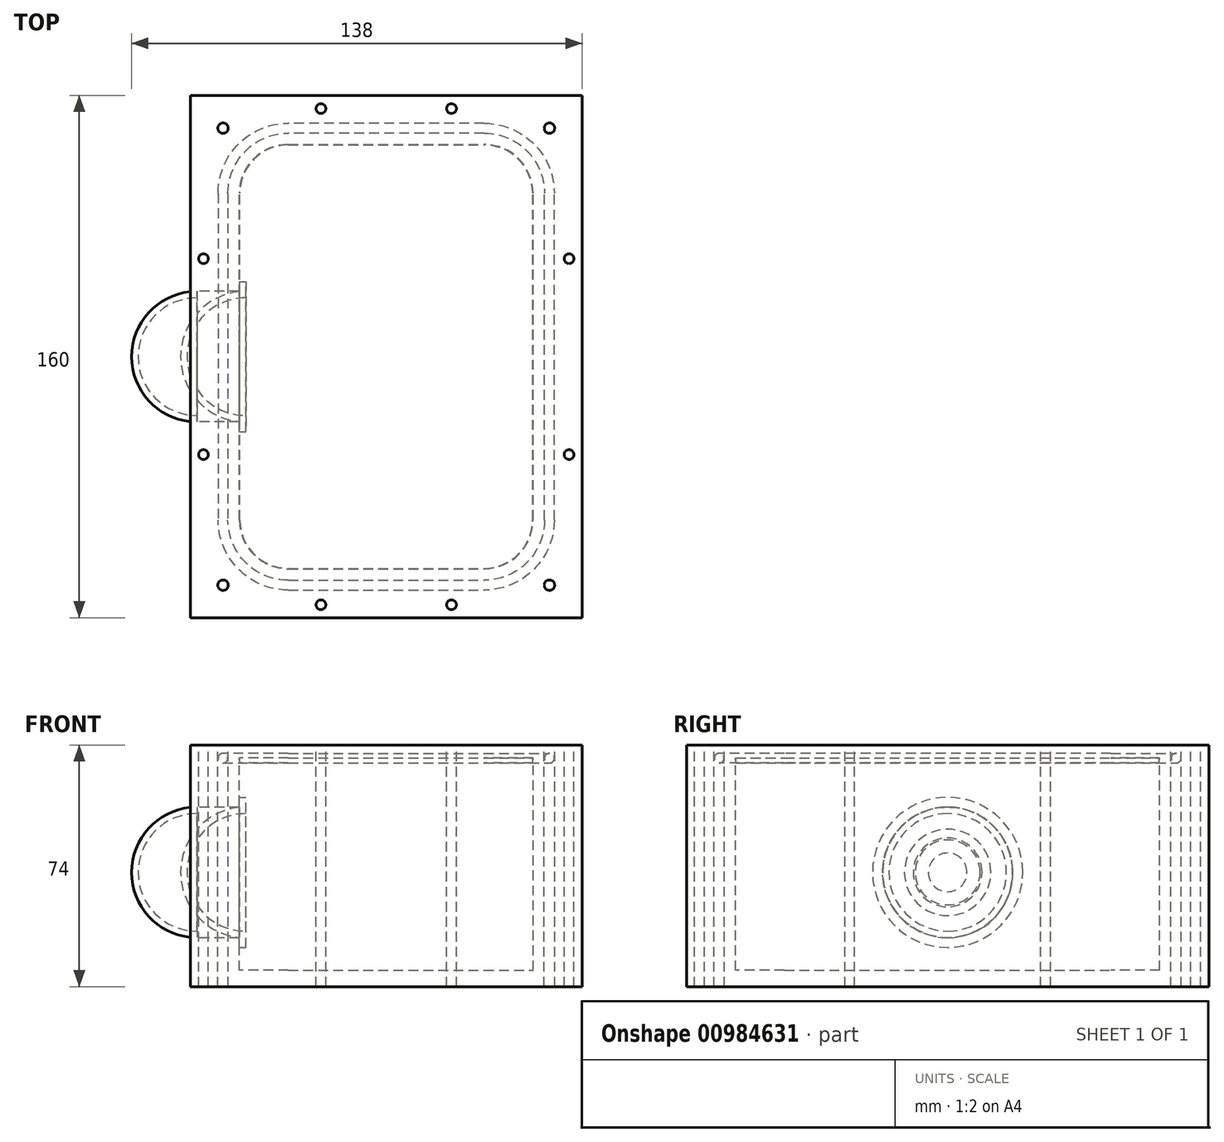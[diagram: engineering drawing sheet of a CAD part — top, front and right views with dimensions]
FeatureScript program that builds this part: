
annotation { "Feature Type Name" : "Feature", "Feature Type Description" : "" }
export const myFeature = defineFeature(function(context is Context, id is Id, definition is map)
    precondition{}
    {
        {
            var Q0;
            Q0=qCreatedBy(makeId("Top.planeOp"),FACE);
            var sketch = newSketch(context, id + "F0", { "sketchPlane" : qUnion([Q0])});
            skLineSegment(sketch, "E0.bottom", {"start": v(-60, -80) * mm, "end": v(60, -80) * mm});
            skLineSegment(sketch, "E0.top", {"start": v(-60, 80) * mm, "end": v(60, 80) * mm});
            skLineSegment(sketch, "E0.left", {"start": v(-60, -80) * mm, "end": v(-60, 80) * mm});
            skLineSegment(sketch, "E0.right", {"start": v(60, -80) * mm, "end": v(60, 80) * mm});
            skSolve(sketch);
        }
        {
            var Q0;
            Q0 = qSketchRegion(id + "F0", true);
            extrude(context, id + "F1", {"entities" : qUnion([Q0]), "oppositeDirection" : true, "depth" : 70 * mm, "offsetDistance" : 25 * mm});
        }
        {
            var Q0;
            Q0=qCreatedBy(makeId("Top.planeOp"),FACE);
            var sketch = newSketch(context, id + "F2", { "sketchPlane" : qUnion([Q0])});
            skLineSegment(sketch, "E1.bottom", {"start": v(-45, -65) * mm, "end": v(45, -65) * mm});
            skLineSegment(sketch, "E1.top", {"start": v(-45, 65) * mm, "end": v(45, 65) * mm});
            skLineSegment(sketch, "E1.left", {"start": v(-45, -65) * mm, "end": v(-45, 65) * mm});
            skLineSegment(sketch, "E1.right", {"start": v(45, -65) * mm, "end": v(45, 65) * mm});
            skSolve(sketch);
        }
        {
            var Q0;
            Q0=makeQuery(id+"F2.imprint","IMPRINT",FACE,{"disambiguationData":[TD([[makeQuery(id+"F2.imprint","IMPRINT",EDGE,{"derivedFrom":sQuery(id+"F2.wireOp",EDGE,"E1.bottom")}),1.0]])]});
            extrude(context, id + "F3", {"entities" : qUnion([Q0]), "operationType" : NewBodyOperationType.REMOVE, "oppositeDirection" : true, "depth" : 65 * mm, "offsetDistance" : 25 * mm});
        }
        {
            var Q0;
            Q0=makeQuery(id+"F3.boolean.opBoolean","COPY",EDGE,{"derivedFrom":makeQuery(id+"F3.opExtrude","SWEPT_EDGE",EDGE,{"disambiguationData":[OSD([sQuery(id+"F2.wireOp",EDGE,"E1.bottom"),sQuery(id+"F2.wireOp",EDGE,"E1.left")])]})});
            var Q1;
            Q1=makeQuery(id+"F3.boolean.opBoolean","COPY",EDGE,{"derivedFrom":makeQuery(id+"F3.opExtrude","SWEPT_EDGE",EDGE,{"disambiguationData":[OSD([sQuery(id+"F2.wireOp",EDGE,"E1.bottom"),sQuery(id+"F2.wireOp",EDGE,"E1.right")])]})});
            var Q2;
            Q2=makeQuery(id+"F3.boolean.opBoolean","COPY",EDGE,{"derivedFrom":makeQuery(id+"F3.opExtrude","SWEPT_EDGE",EDGE,{"disambiguationData":[OSD([sQuery(id+"F2.wireOp",EDGE,"E1.top"),sQuery(id+"F2.wireOp",EDGE,"E1.right")])]})});
            var Q3;
            Q3=makeQuery(id+"F3.boolean.opBoolean","COPY",EDGE,{"derivedFrom":makeQuery(id+"F3.opExtrude","SWEPT_EDGE",EDGE,{"disambiguationData":[OSD([sQuery(id+"F2.wireOp",EDGE,"E1.top"),sQuery(id+"F2.wireOp",EDGE,"E1.left")])]})});
            fillet(context, id + "F4", {"entities" : qUnion([Q0, Q1, Q2, Q3]), "radius" : 15 * mm, "tangentPropagation" : true, "allowEdgeOverflow" : false});
        }
        {
            var Q0;
            Q0=makeQuery(id+"F1.opExtrude","CAP_FACE",FACE,{"disambiguationData":[OSD([sQuery(id+"F0.wireOp",EDGE,"E0.bottom"),sQuery(id+"F0.wireOp",EDGE,"E0.top"),sQuery(id+"F0.wireOp",EDGE,"E0.left"),sQuery(id+"F0.wireOp",EDGE,"E0.right")])],"isStart":true});
            var sketch = newSketch(context, id + "F5", { "sketchPlane" : qUnion([Q0])});
            skArc(sketch, "E2.0", {"start": v(-30, -70) * mm, "mid": v(-44.14, -64.14) * mm, "end": v(-50, -50) * mm});
            skLineSegment(sketch, "E2.1", {"start": v(-30, -70) * mm, "end": v(30, -70) * mm});
            skLineSegment(sketch, "E2.2", {"start": v(-50, -50) * mm, "end": v(-50, 50) * mm});
            skArc(sketch, "E2.3", {"start": v(50, -50) * mm, "mid": v(44.14, -64.14) * mm, "end": v(30, -70) * mm});
            skArc(sketch, "E2.4", {"start": v(-50, 50) * mm, "mid": v(-44.14, 64.14) * mm, "end": v(-30, 70) * mm});
            skLineSegment(sketch, "E2.5", {"start": v(-30, 70) * mm, "end": v(30, 70) * mm});
            skArc(sketch, "E2.6", {"start": v(30, 70) * mm, "mid": v(44.14, 64.14) * mm, "end": v(50, 50) * mm});
            skLineSegment(sketch, "E2.7", {"start": v(50, -50) * mm, "end": v(50, 50) * mm});
            skSolve(sketch);
        }
        {
            var Q0;
            Q0=qCreatedBy(makeId("Front.planeOp"),FACE);
            var sketch = newSketch(context, id + "F6", { "sketchPlane" : qUnion([Q0])});
            skCircle(sketch, "E3", {"center": v(-50, 0) * mm, "radius": 1.5 * mm});
            skSolve(sketch);
        }
        {
            var Q0;
            Q0 = qSketchRegion(id + "F6", true);
            var Q1;
            Q1 = qConstructionFilter(qBodyType(qCreatedBy(id + "F5" ,EDGE), BodyType.WIRE), ConstructionObject.NO);
            sweep(context, id + "F7", {"operationType" : NewBodyOperationType.REMOVE, "profiles" : qUnion([Q0]), "path" : qUnion([Q1])});
        }
        {
            var Q0;
            {var subQ1=sQuery(id+"F0.wireOp",EDGE,"E0.top");var subQ2=sQuery(id+"F0.wireOp",EDGE,"E0.bottom");var subQ3=sQuery(id+"F0.wireOp",EDGE,"E0.right");var subQ4=sQuery(id+"F0.wireOp",EDGE,"E0.left");Q0=makeQuery(id+"F7.boolean.opBoolean","SPLIT",FACE,{"disambiguationData":[TD([makeQuery(id+"F1.opExtrude","SWEPT_FACE",FACE,{"disambiguationData":[OSD([subQ2])]})])],"derivedFrom":makeQuery(id+"F1.opExtrude","CAP_FACE",FACE,{"disambiguationData":[OSD([subQ2,subQ1,subQ4,subQ3])],"isStart":true})});}
            var sketch = newSketch(context, id + "F8", { "sketchPlane" : qUnion([Q0])});
            skCircle(sketch, "E4", {"center": v(50, 70) * mm, "radius": 1.6 * mm});
            skCircle(sketch, "E5.MirrorC", {"center": v(50, -70) * mm, "radius": 1.6 * mm});
            skCircle(sketch, "E6.MirrorC", {"center": v(-50, -70) * mm, "radius": 1.6 * mm});
            skCircle(sketch, "E7.MirrorC", {"center": v(-50, 70) * mm, "radius": 1.6 * mm});
            skCircle(sketch, "E8", {"center": v(56, 30) * mm, "radius": 1.5 * mm});
            skCircle(sketch, "E9", {"center": v(20, 76) * mm, "radius": 1.5 * mm});
            skCircle(sketch, "E10.MirrorC", {"center": v(56, -30) * mm, "radius": 1.5 * mm});
            skCircle(sketch, "E11.MirrorC", {"center": v(20, -76) * mm, "radius": 1.5 * mm});
            skCircle(sketch, "E12.MirrorC", {"center": v(-20, 76) * mm, "radius": 1.5 * mm});
            skCircle(sketch, "E13.MirrorC", {"center": v(-56, 30) * mm, "radius": 1.5 * mm});
            skCircle(sketch, "E14.MirrorC", {"center": v(-56, -30) * mm, "radius": 1.5 * mm});
            skCircle(sketch, "E15.MirrorC", {"center": v(-20, -76) * mm, "radius": 1.5 * mm});
            skSolve(sketch);
        }
        {
            var Q0;
            Q0 = qSketchRegion(id + "F8", true);
            extrude(context, id + "F9", {"entities" : qUnion([Q0]), "operationType" : NewBodyOperationType.REMOVE, "endBound" : BoundingType.SYMMETRIC, "oppositeDirection" : true, "depth" : 200 * mm, "offsetDistance" : 25 * mm});
        }
        {
            var Q0;
            Q0=makeQuery(id+"F1.opExtrude","SWEPT_FACE",FACE,{"disambiguationData":[OSD([sQuery(id+"F0.wireOp",EDGE,"E0.left")])]});
            var sketch = newSketch(context, id + "F10", { "sketchPlane" : qUnion([Q0])});
            skCircle(sketch, "E16", {"center": v(0, -35) * mm, "radius": 20 * mm});
            skSolve(sketch);
        }
        {
            var Q0;
            Q0 = qSketchRegion(id + "F10", true);
            extrude(context, id + "F11", {"entities" : qUnion([Q0]), "operationType" : NewBodyOperationType.REMOVE, "oppositeDirection" : true, "depth" : 25 * mm, "offsetDistance" : 25 * mm});
        }
        {
            var Q0;
            Q0=makeQuery(id+"F3.boolean.opBoolean","COPY",FACE,{"derivedFrom":makeQuery(id+"F3.opExtrude","SWEPT_FACE",FACE,{"disambiguationData":[OSD([sQuery(id+"F2.wireOp",EDGE,"E1.left")])]})});
            cPlane(context, id + "F12", {"entities" : qUnion([Q0]), "cplaneType" : CPlaneType.OFFSET, "offset" : 2 * mm, "width" : 150 * mm, "height" : 150 * mm});
        }
        {
            var Q0;
            Q0=qCreatedBy(id+"F12.planeOp",FACE);
            var sketch = newSketch(context, id + "F13", { "sketchPlane" : qUnion([Q0])});
            skArc(sketch, "E17", {"start": v(0, -15) * mm, "mid": v(-20, -35) * mm, "end": v(0, -55) * mm});
            skArc(sketch, "E18", {"start": v(0, -17) * mm, "mid": v(-18, -35) * mm, "end": v(0, -53) * mm});
            skLineSegment(sketch, "E19", {"start": v(0, -17) * mm, "end": v(0, -15) * mm});
            skLineSegment(sketch, "E20", {"start": v(0, -53) * mm, "end": v(0, -55) * mm});
            skSolve(sketch);
        }
        {
            var Q0;
            Q0 = qSketchRegion(id + "F13", true);
            var Q1;
            Q1=sQuery(id+"F13.wireOp",EDGE,"E19");
            revolve(context, id + "F14", {"surfaceOperationType" : NewSurfaceOperationType.NEW, "entities" : qUnion([Q0]), "axis" : qUnion([Q1]), "revolveType" : RevolveType.ONE_DIRECTION, "oppositeDirection" : true, "angle" : 180 * degree});
        }
        {
            var Q0;
            Q0=qCreatedBy(id+"F12.planeOp",FACE);
            var sketch = newSketch(context, id + "F15", { "sketchPlane" : qUnion([Q0])});
            skCircle(sketch, "E21", {"center": v(0, -35) * mm, "radius": 19 * mm});
            skCircle(sketch, "E22", {"center": v(0, -35) * mm, "radius": 23 * mm});
            skSolve(sketch);
        }
        {
            var Q0;
            Q0 = qSketchRegion(id + "F15", true);
            extrude(context, id + "F16", {"entities" : qUnion([Q0]), "operationType" : NewBodyOperationType.ADD, "oppositeDirection" : true, "depth" : 2 * mm, "offsetDistance" : 25 * mm});
        }
        {
            var Q0;
            Q0=makeQuery(id+"F1.opExtrude","SWEPT_FACE",FACE,{"disambiguationData":[OSD([sQuery(id+"F0.wireOp",EDGE,"E0.left")])]});
            var sketch = newSketch(context, id + "F17", { "sketchPlane" : qUnion([Q0])});
            skCircle(sketch, "E23", {"center": v(0, -35) * mm, "radius": 23 * mm});
            skSolve(sketch);
        }
        {
            var Q0;
            Q0=makeQuery(id+"F1.opExtrude","SWEPT_BODY",BODY,{"disambiguationData":[OSD([sQuery(id+"F0.wireOp",EDGE,"E0.bottom"),sQuery(id+"F0.wireOp",EDGE,"E0.top"),sQuery(id+"F0.wireOp",EDGE,"E0.left"),sQuery(id+"F0.wireOp",EDGE,"E0.right")])]});
            transform(context, id + "F18", {"entities" : qUnion([Q0]), "transformType" : TransformType.TRANSLATION_3D, "dx" : 0 * mm, "dy" : 0 * mm, "dz" : 0 * mm, "makeCopy" : true});
        }
        {
            var Q0;
            Q0 = qSketchRegion(id + "F17", true);
            extrude(context, id + "F19", {"entities" : qUnion([Q0]), "operationType" : NewBodyOperationType.REMOVE, "oppositeDirection" : true, "depth" : 2 * mm, "offsetDistance" : 25 * mm});
        }
        {
            var Q0;
            Q0=makeQuery(id+"F19.boolean.opBoolean","COPY",FACE,{"derivedFrom":makeQuery(id+"F19.opExtrude","CAP_FACE",FACE,{"disambiguationData":[OSD([sQuery(id+"F17.wireOp",EDGE,"E23")])],"isStart":false})});
            var sketch = newSketch(context, id + "F20", { "sketchPlane" : qUnion([Q0])});
            skArc(sketch, "E24", {"start": v(0, -15) * mm, "mid": v(-20, -35) * mm, "end": v(0, -55) * mm});
            skArc(sketch, "E25", {"start": v(0, -17) * mm, "mid": v(-18, -35) * mm, "end": v(0, -53) * mm});
            skLineSegment(sketch, "E26", {"start": v(0, -15) * mm, "end": v(0, -17) * mm});
            skLineSegment(sketch, "E27", {"start": v(0, -55) * mm, "end": v(0, -53) * mm});
            skSolve(sketch);
        }
        {
            var Q0;
            Q0 = qSketchRegion(id + "F20", true);
            var Q1;
            Q1=sQuery(id+"F20.wireOp",EDGE,"E27");
            revolve(context, id + "F21", {"surfaceOperationType" : NewSurfaceOperationType.NEW, "entities" : qUnion([Q0]), "axis" : qUnion([Q1]), "revolveType" : RevolveType.ONE_DIRECTION, "angle" : 180 * degree});
        }
        {
            var Q0;
            Q0=makeQuery(id+"F19.boolean.opBoolean","COPY",FACE,{"derivedFrom":makeQuery(id+"F19.opExtrude","CAP_FACE",FACE,{"disambiguationData":[OSD([sQuery(id+"F17.wireOp",EDGE,"E23")])],"isStart":false})});
            var sketch = newSketch(context, id + "F22", { "sketchPlane" : qUnion([Q0])});
            skCircle(sketch, "E28", {"center": v(0, -35) * mm, "radius": 19 * mm});
            skCircle(sketch, "E29", {"center": v(0, -35) * mm, "radius": 23 * mm});
            skSolve(sketch);
        }
        {
            var Q0;
            Q0 = qSketchRegion(id + "F22", true);
            extrude(context, id + "F23", {"entities" : qUnion([Q0]), "operationType" : NewBodyOperationType.ADD, "depth" : 2 * mm, "offsetDistance" : 25 * mm});
        }
        {
            var Q0;
            Q0=qCreatedBy(makeId("Top.planeOp"),FACE);
            var sketch = newSketch(context, id + "F24", { "sketchPlane" : qUnion([Q0])});
            skLineSegment(sketch, "E30.0", {"start": v(-44.85, -50) * mm, "end": v(-44.85, 50) * mm});
            skArc(sketch, "E30.1", {"start": v(-30, -64.85) * mm, "mid": v(-40.5, -60.5) * mm, "end": v(-44.85, -50) * mm});
            skArc(sketch, "E30.2", {"start": v(-44.85, 50) * mm, "mid": v(-40.5, 60.5) * mm, "end": v(-30, 64.85) * mm});
            skLineSegment(sketch, "E30.3", {"start": v(-30, -64.85) * mm, "end": v(30, -64.85) * mm});
            skLineSegment(sketch, "E30.4", {"start": v(-30, 64.85) * mm, "end": v(30, 64.85) * mm});
            skArc(sketch, "E30.5", {"start": v(30, 64.85) * mm, "mid": v(40.5, 60.5) * mm, "end": v(44.85, 50) * mm});
            skLineSegment(sketch, "E30.6", {"start": v(44.85, -50) * mm, "end": v(44.85, 50) * mm});
            skArc(sketch, "E30.7", {"start": v(44.85, -50) * mm, "mid": v(40.5, -60.5) * mm, "end": v(30, -64.85) * mm});
            skSolve(sketch);
        }
        {
            var Q0;
            Q0 = qSketchRegion(id + "F24", true);
            extrude(context, id + "F25", {"entities" : qUnion([Q0]), "oppositeDirection" : true, "depth" : 1.5 * mm, "offsetDistance" : 25 * mm});
        }
        {
            var Q0;
            Q0=qCreatedBy(makeId("Top.planeOp"),FACE);
            var sketch = newSketch(context, id + "F26", { "sketchPlane" : qUnion([Q0])});
            skLineSegment(sketch, "E31.bottom", {"start": v(-60, 80) * mm, "end": v(60, 80) * mm});
            skLineSegment(sketch, "E31.top", {"start": v(-60, -80) * mm, "end": v(60, -80) * mm});
            skLineSegment(sketch, "E31.left", {"start": v(-60, 80) * mm, "end": v(-60, -80) * mm});
            skLineSegment(sketch, "E31.right", {"start": v(60, 80) * mm, "end": v(60, -80) * mm});
            skSolve(sketch);
        }
        {
            var Q0;
            Q0 = qSketchRegion(id + "F26", true);
            extrude(context, id + "F27", {"entities" : qUnion([Q0]), "operationType" : NewBodyOperationType.ADD, "depth" : 4 * mm, "offsetDistance" : 25 * mm});
        }
        {
            var Q0;
            Q0 = qSketchRegion(id + "F8", true);
            extrude(context, id + "F28", {"entities" : qUnion([Q0]), "operationType" : NewBodyOperationType.REMOVE, "depth" : 25 * mm, "offsetDistance" : 25 * mm});
        }
        {
            var Q0;
            Q0 = qSketchRegion(id + "F6", true);
            var Q1;
            Q1 = qConstructionFilter(qBodyType(qCreatedBy(id + "F5" ,EDGE), BodyType.WIRE), ConstructionObject.NO);
            sweep(context, id + "F29", {"operationType" : NewBodyOperationType.REMOVE, "profiles" : qUnion([Q0]), "path" : qUnion([Q1])});
        }
    });
